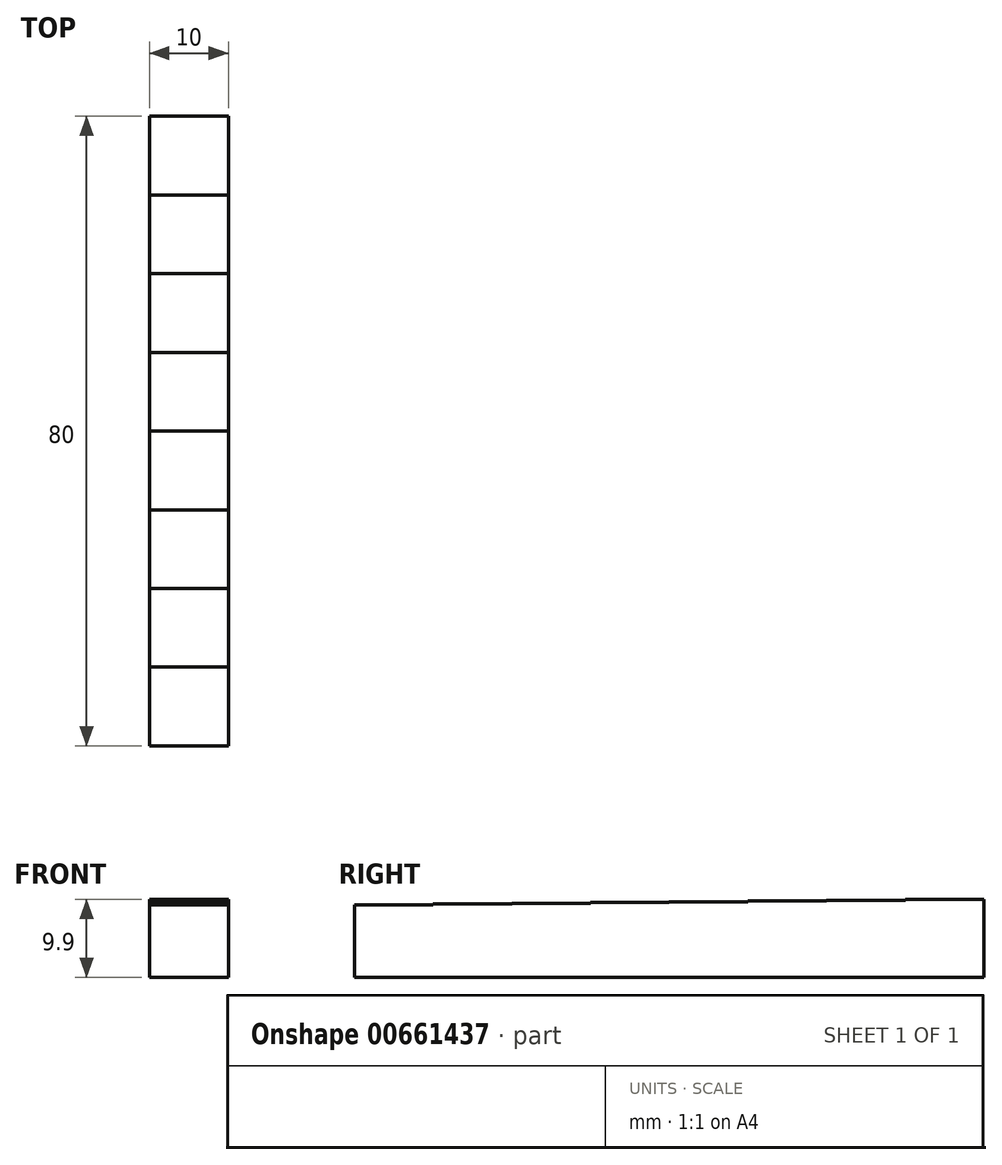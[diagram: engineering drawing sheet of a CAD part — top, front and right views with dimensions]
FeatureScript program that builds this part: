
annotation { "Feature Type Name" : "Feature", "Feature Type Description" : "" }
export const myFeature = defineFeature(function(context is Context, id is Id, definition is map)
    precondition{}
    {
        {
            var Q0;
            Q0=qCreatedBy(makeId("Right.planeOp"),FACE);
            var sketch = newSketch(context, id + "F0", { "sketchPlane" : qUnion([Q0])});
            skLineSegment(sketch, "E0", {"start": v(0, 0) * mm, "end": v(0, 9.2) * mm});
            skLineSegment(sketch, "E1", {"start": v(0, 9.2) * mm, "end": v(10, 9.2) * mm});
            skLineSegment(sketch, "E2", {"start": v(10, 9.2) * mm, "end": v(10, 9.3) * mm});
            skLineSegment(sketch, "E3", {"start": v(10, 9.3) * mm, "end": v(20, 9.3) * mm});
            skLineSegment(sketch, "E4", {"start": v(20, 9.3) * mm, "end": v(20, 9.4) * mm});
            skLineSegment(sketch, "E5", {"start": v(20, 9.4) * mm, "end": v(30, 9.4) * mm});
            skLineSegment(sketch, "E6", {"start": v(30, 9.4) * mm, "end": v(30, 9.5) * mm});
            skLineSegment(sketch, "E7", {"start": v(30, 9.5) * mm, "end": v(40, 9.5) * mm});
            skLineSegment(sketch, "E8", {"start": v(40, 9.5) * mm, "end": v(40, 9.6) * mm});
            skLineSegment(sketch, "E9", {"start": v(40, 9.6) * mm, "end": v(50, 9.6) * mm});
            skLineSegment(sketch, "E10", {"start": v(50, 9.6) * mm, "end": v(50, 9.7) * mm});
            skLineSegment(sketch, "E11", {"start": v(50, 9.7) * mm, "end": v(60, 9.7) * mm});
            skLineSegment(sketch, "E12", {"start": v(60, 9.7) * mm, "end": v(60, 9.8) * mm});
            skLineSegment(sketch, "E13", {"start": v(60, 9.8) * mm, "end": v(70, 9.8) * mm});
            skLineSegment(sketch, "E14", {"start": v(70, 9.8) * mm, "end": v(70, 9.9) * mm});
            skLineSegment(sketch, "E15", {"start": v(70, 9.9) * mm, "end": v(80, 9.9) * mm});
            skLineSegment(sketch, "E16", {"start": v(80, 9.9) * mm, "end": v(80, 0) * mm});
            skLineSegment(sketch, "E17", {"start": v(80, 0) * mm, "end": v(0, 0) * mm});
            skSolve(sketch);
        }
        {
            var Q0;
            Q0=qSketchRegion(id+"F0",true);
            extrude(context, id + "F1", {"entities" : qUnion([Q0]), "depth" : 10 * mm, "offsetDistance" : 25 * mm});
        }
    });
